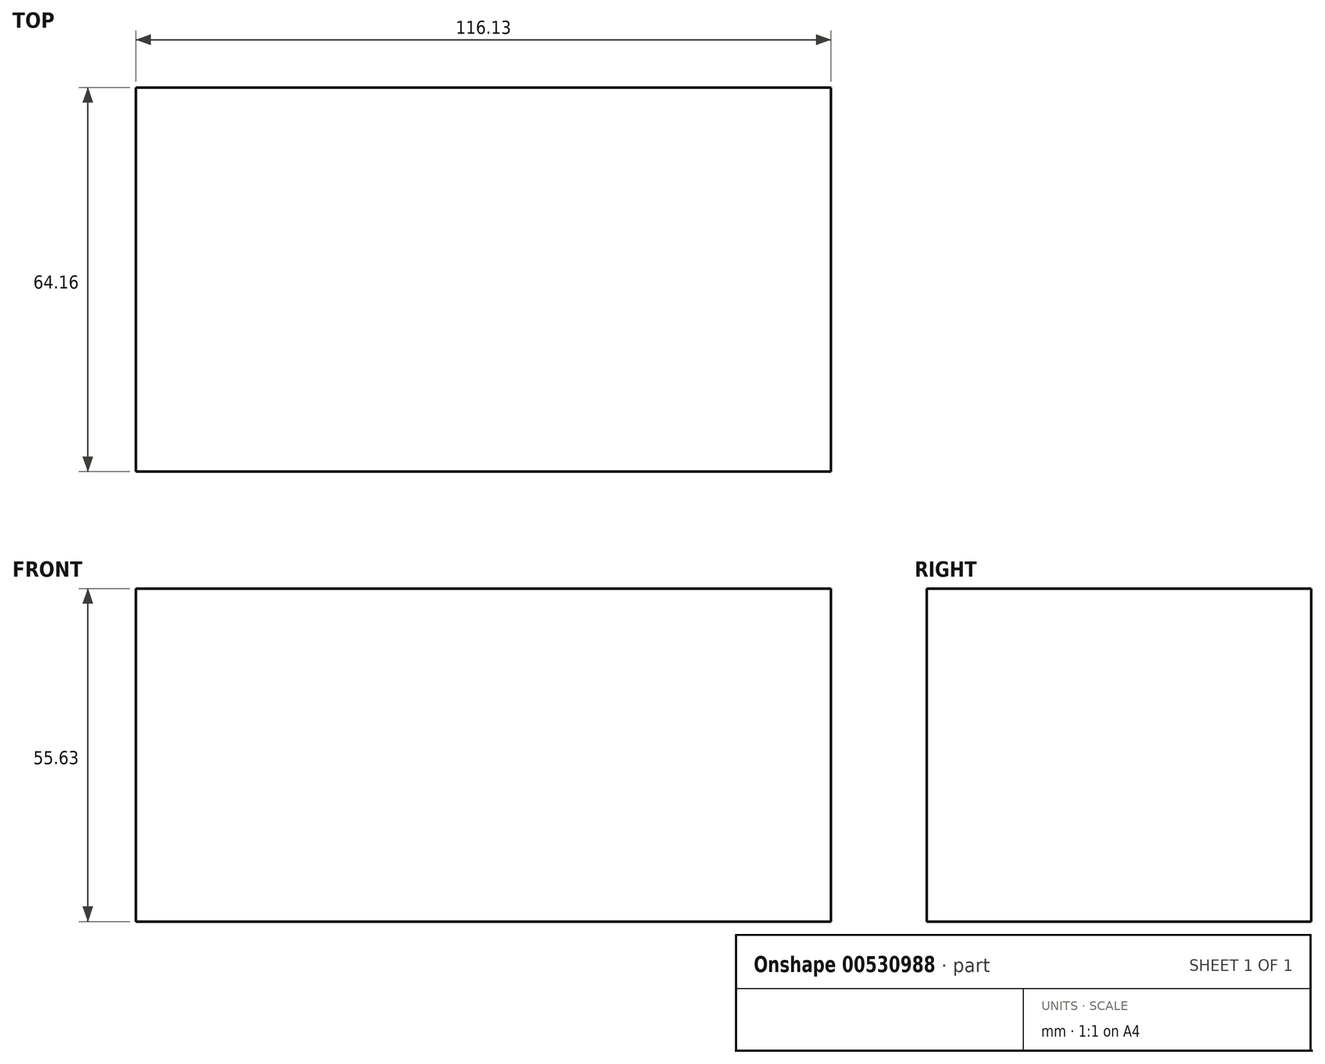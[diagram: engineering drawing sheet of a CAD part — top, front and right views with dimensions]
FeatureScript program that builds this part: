
annotation { "Feature Type Name" : "Feature", "Feature Type Description" : "" }
export const myFeature = defineFeature(function(context is Context, id is Id, definition is map)
    precondition{}
    {
        {
            var Q0;
            Q0=qCreatedBy(makeId("Top.planeOp"),FACE);
            var sketch = newSketch(context, id + "F0", { "sketchPlane" : qUnion([Q0])});
            skLineSegment(sketch, "E0.bottom", {"start": v(-59.79, 28.84) * mm, "end": v(56.34, 28.84) * mm});
            skLineSegment(sketch, "E0.top", {"start": v(-59.79, -35.32) * mm, "end": v(56.34, -35.32) * mm});
            skLineSegment(sketch, "E0.left", {"start": v(-59.79, 28.84) * mm, "end": v(-59.79, -35.32) * mm});
            skLineSegment(sketch, "E0.right", {"start": v(56.34, 28.84) * mm, "end": v(56.34, -35.32) * mm});
            skSolve(sketch);
        }
        {
            var Q0;
            Q0 = qSketchRegion(id + "F0", true);
            extrude(context, id + "F1", {"entities" : qUnion([Q0]), "depth" : 55.63 * mm, "offsetDistance" : 25.4 * mm});
        }
    });
